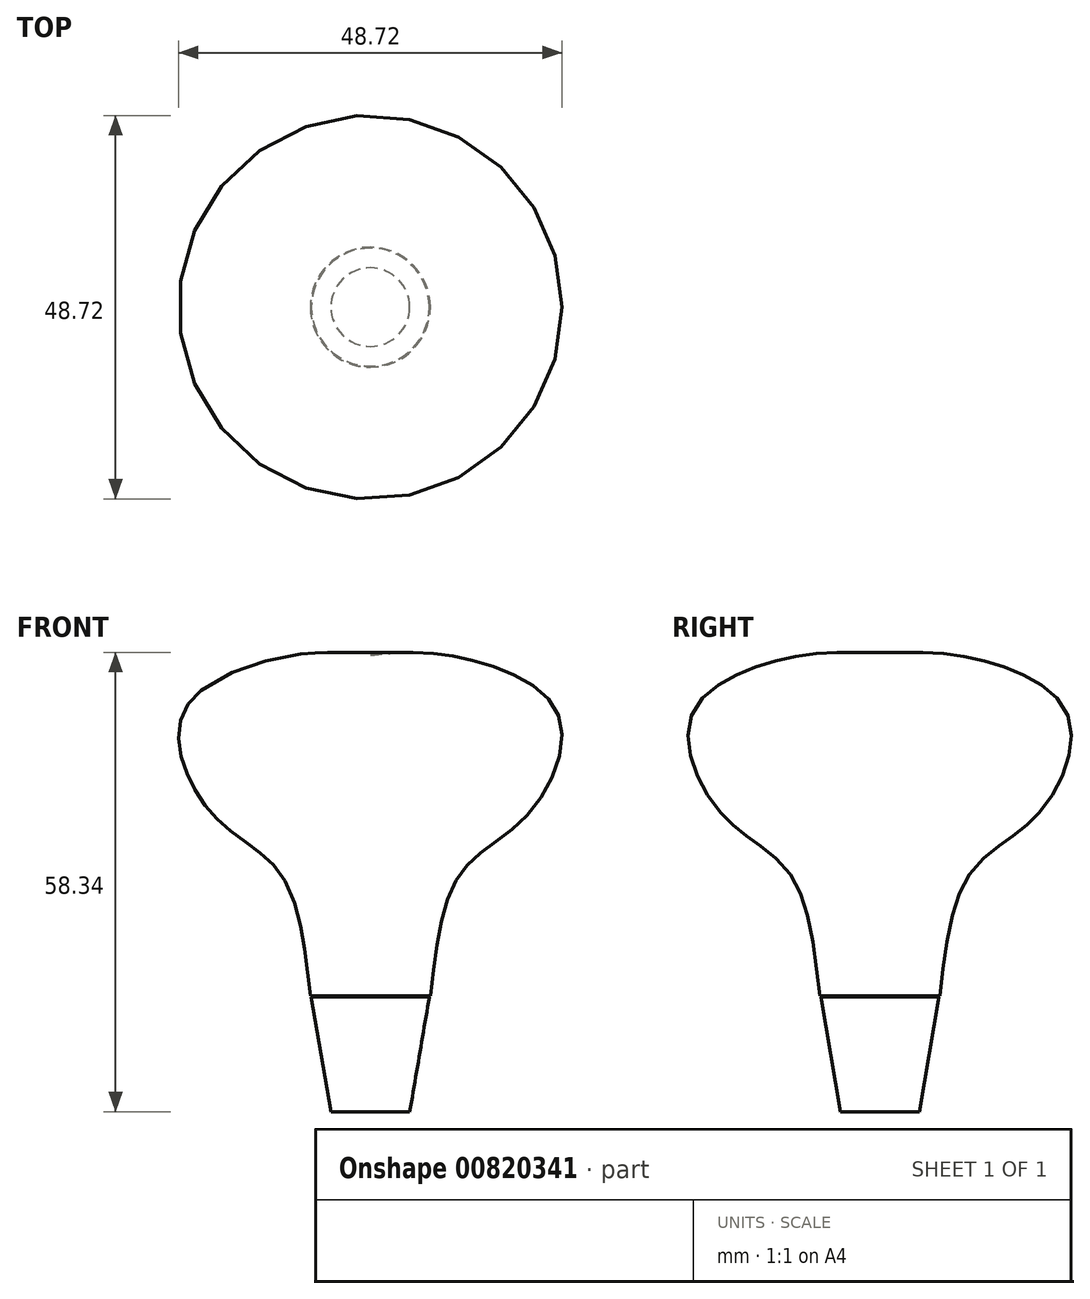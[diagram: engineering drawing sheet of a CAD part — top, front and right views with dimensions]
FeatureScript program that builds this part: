
annotation { "Feature Type Name" : "Feature", "Feature Type Description" : "" }
export const myFeature = defineFeature(function(context is Context, id is Id, definition is map)
    precondition{}
    {
        {
            var Q0;
            Q0=qCreatedBy(makeId("Top.planeOp"),FACE);
            var sketch = newSketch(context, id + "F0", { "sketchPlane" : qUnion([Q0])});
            skCircle(sketch, "E0", {"center": v(0, 0) * mm, "radius": 5 * mm});
            skSolve(sketch);
        }
        {
            var Q0;
            Q0=qCreatedBy(makeId("Top.planeOp"),FACE);
            cPlane(context, id + "F1", {"entities" : qUnion([Q0]), "cplaneType" : CPlaneType.OFFSET, "offset" : 14.6 * mm, "width" : 150 * mm, "height" : 150 * mm});
        }
        {
            var Q0;
            Q0=qCreatedBy(id+"F1.planeOp",FACE);
            var sketch = newSketch(context, id + "F2", { "sketchPlane" : qUnion([Q0])});
            skCircle(sketch, "E1", {"center": v(0, 0) * mm, "radius": 7.5 * mm});
            skSolve(sketch);
        }
        {
            var Q0;
            Q0=makeQuery(id+"F0.imprint","IMPRINT",FACE,{"disambiguationData":[TD([[makeQuery(id+"F0.imprint","IMPRINT",EDGE,{"derivedFrom":sQuery(id+"F0.wireOp",EDGE,"E0")}),1.0]])]});
            var Q1;
            Q1=makeQuery(id+"F2.imprint","IMPRINT",FACE,{"disambiguationData":[TD([[makeQuery(id+"F2.imprint","IMPRINT",EDGE,{"derivedFrom":sQuery(id+"F2.wireOp",EDGE,"E1")}),1.0]])]});
            loft(context, id + "F3", {"sheetProfilesArray" : [{ "sheetProfileEntities" : qUnion([Q0]) }, { "sheetProfileEntities" : qUnion([Q1]) }]});
        }
        {
            var Q0;
            Q0=qCreatedBy(makeId("Front.planeOp"),FACE);
            var sketch = newSketch(context, id + "F4", { "sketchPlane" : qUnion([Q0])});
            skLineSegment(sketch, "E2", {"start": v(0, 10.21) * mm, "end": v(0, 64.37) * mm, "construction": true});
            skFitSpline(sketch, "E3", {"points": [v(0, 57.98) * mm, v(13.5, 57.2) * mm, v(23.93, 50.31) * mm, v(20, 37.72) * mm, v(11.45, 30.3) * mm, v(7.62, 14.72) * mm], "startDerivative": vector(83.47, 9.6) * mm, "endDerivative": vector(-9.8, -82.21) * mm});
            skLineSegment(sketch, "E4", {"start": v(0, 57.98) * mm, "end": v(0, 14.72) * mm});
            skLineSegment(sketch, "E5", {"start": v(0, 14.72) * mm, "end": v(7.62, 14.72) * mm});
            skSolve(sketch);
        }
        {
            var Q0;
            Q0=makeQuery(id+"F4.imprint","IMPRINT",FACE,{"disambiguationData":[TD([[makeQuery(id+"F4.imprint","IMPRINT",EDGE,{"derivedFrom":sQuery(id+"F4.wireOp",EDGE,"E3")}),-1.0]])]});
            var Q1;
            Q1=sQuery(id+"F4.wireOp",EDGE,"E2");
            revolve(context, id + "F5", {"surfaceOperationType" : NewSurfaceOperationType.NEW, "entities" : qUnion([Q0]), "axis" : qUnion([Q1]), "revolveType" : RevolveType.FULL});
        }
    });
